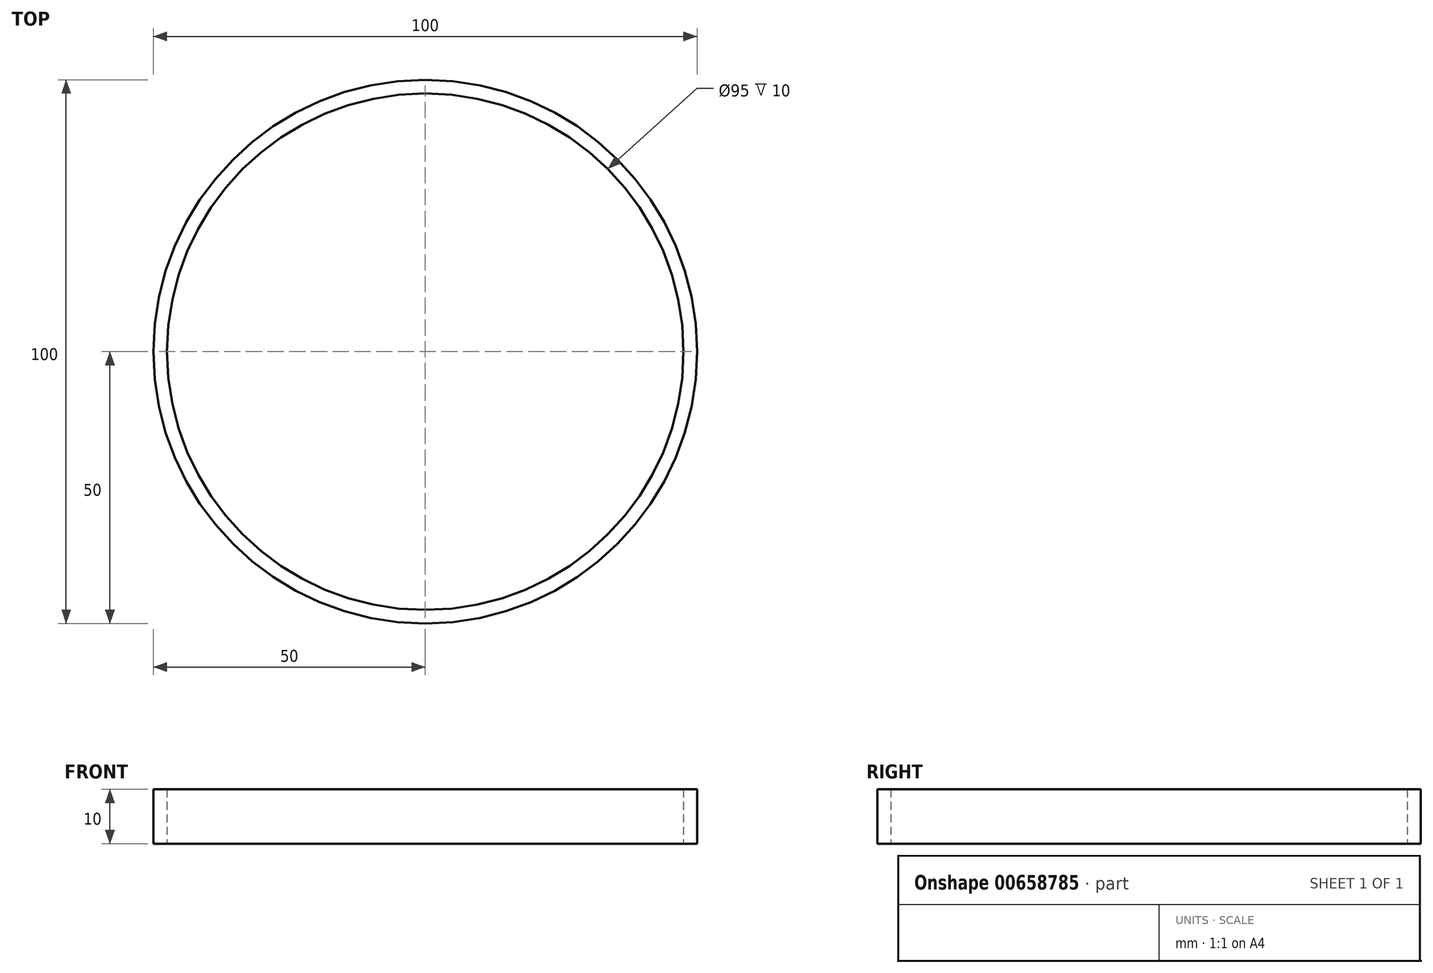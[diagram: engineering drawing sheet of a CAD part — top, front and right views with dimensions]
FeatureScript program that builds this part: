
annotation { "Feature Type Name" : "Feature", "Feature Type Description" : "" }
export const myFeature = defineFeature(function(context is Context, id is Id, definition is map)
    precondition{}
    {
        {
            var Q0;
            Q0=qCreatedBy(makeId("Top.planeOp"),FACE);
            var sketch = newSketch(context, id + "F0", { "sketchPlane" : qUnion([Q0])});
            skCircle(sketch, "E0", {"center": v(0, 0) * mm, "radius": 50 * mm});
            skCircle(sketch, "E1", {"center": v(0, 0) * mm, "radius": 47.5 * mm});
            skSolve(sketch);
        }
        {
            var Q0;
            Q0 = qSketchRegion(id + "F0", true);
            extrude(context, id + "F1", {"entities" : qUnion([Q0]), "depth" : 10 * mm, "offsetDistance" : 25 * mm});
        }
    });
